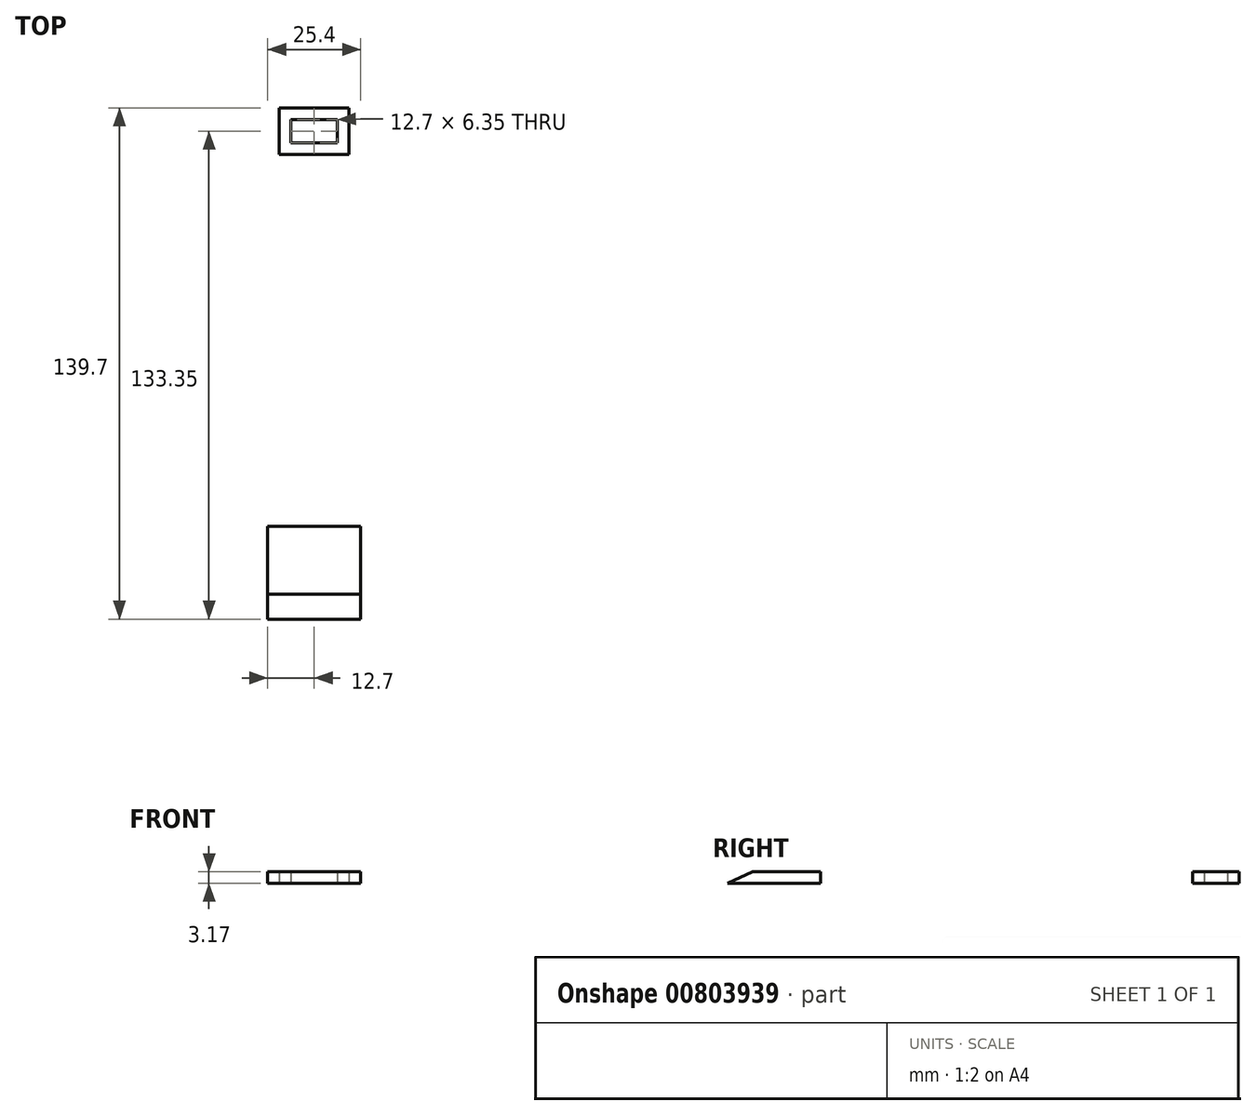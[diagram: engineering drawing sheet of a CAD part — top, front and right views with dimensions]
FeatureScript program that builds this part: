
annotation { "Feature Type Name" : "Feature", "Feature Type Description" : "" }
export const myFeature = defineFeature(function(context is Context, id is Id, definition is map)
    precondition{}
    {
        {
            var Q0;
            Q0=qCreatedBy(makeId("Top.planeOp"),FACE);
            var sketch = newSketch(context, id + "F0", { "sketchPlane" : qUnion([Q0])});
            skLineSegment(sketch, "E0", {"start": v(0, 139.7) * mm, "end": v(0, 0) * mm, "construction": true});
            skLineSegment(sketch, "E1.bottom", {"start": v(-12.7, 0) * mm, "end": v(12.7, 0) * mm});
            skLineSegment(sketch, "E1.top", {"start": v(-12.7, 25.4) * mm, "end": v(12.7, 25.4) * mm});
            skLineSegment(sketch, "E1.left", {"start": v(-12.7, 0) * mm, "end": v(-12.7, 25.4) * mm});
            skLineSegment(sketch, "E1.right", {"start": v(12.7, 0) * mm, "end": v(12.7, 25.4) * mm});
            skLineSegment(sketch, "E2.bottom", {"start": v(-6.35, 25.4) * mm, "end": v(6.35, 25.4) * mm});
            skLineSegment(sketch, "E2.top", {"start": v(-6.35, 127) * mm, "end": v(6.35, 127) * mm});
            skLineSegment(sketch, "E2.left", {"start": v(-6.35, 25.4) * mm, "end": v(-6.35, 127) * mm});
            skLineSegment(sketch, "E2.right", {"start": v(6.35, 25.4) * mm, "end": v(6.35, 127) * mm});
            skLineSegment(sketch, "E3.bottom", {"start": v(-9.53, 139.7) * mm, "end": v(9.53, 139.7) * mm});
            skLineSegment(sketch, "E3.top", {"start": v(-9.53, 127) * mm, "end": v(9.52, 127) * mm});
            skLineSegment(sketch, "E3.left", {"start": v(-9.53, 139.7) * mm, "end": v(-9.53, 127) * mm});
            skLineSegment(sketch, "E3.right", {"start": v(9.52, 139.7) * mm, "end": v(9.52, 127) * mm});
            skLineSegment(sketch, "E4.bottom", {"start": v(-6.35, 130.18) * mm, "end": v(6.35, 130.18) * mm});
            skLineSegment(sketch, "E4.top", {"start": v(-6.35, 136.52) * mm, "end": v(6.35, 136.52) * mm});
            skLineSegment(sketch, "E4.left", {"start": v(-6.35, 130.18) * mm, "end": v(-6.35, 136.52) * mm});
            skLineSegment(sketch, "E4.right", {"start": v(6.35, 130.18) * mm, "end": v(6.35, 136.52) * mm});
            skSolve(sketch);
        }
        {
            var Q0;
            Q0=makeQuery(id+"F0.imprint","IMPRINT",FACE,{"disambiguationData":[TD([[makeQuery(id+"F0.imprint","IMPRINT",EDGE,{"derivedFrom":sQuery(id+"F0.wireOp",EDGE,"E2.bottom")}),1.0]])]});
            var Q1;
            Q1=makeQuery(id+"F0.imprint","IMPRINT",FACE,{"disambiguationData":[TD([[makeQuery(id+"F0.imprint","IMPRINT",EDGE,{"derivedFrom":sQuery(id+"F0.wireOp",EDGE,"E3.bottom")}),-1.0]])]});
            var Q2;
            Q2=makeQuery(id+"F0.imprint","IMPRINT",FACE,{"disambiguationData":[TD([[makeQuery(id+"F0.imprint","IMPRINT",EDGE,{"derivedFrom":sQuery(id+"F0.wireOp",EDGE,"E1.bottom")}),1.0]])]});
            extrude(context, id + "F1", {"entities" : qUnion([Q0, Q1, Q2]), "depth" : 3.17 * mm, "offsetDistance" : 25.4 * mm});
        }
        {
            var Q0;
            Q0=makeQuery(id+"F1.opExtrude","SWEPT_FACE",FACE,{"disambiguationData":[OSD([sQuery(id+"F0.wireOp",EDGE,"E1.right")])]});
            var sketch = newSketch(context, id + "F2", { "sketchPlane" : qUnion([Q0])});
            skLineSegment(sketch, "E5", {"start": v(0, 0) * mm, "end": v(6.8, 3.18) * mm});
            skLineSegment(sketch, "E6", {"start": v(0, 0) * mm, "end": v(0, 3.18) * mm});
            skLineSegment(sketch, "E7", {"start": v(0, 3.17) * mm, "end": v(6.8, 3.17) * mm});
            skSolve(sketch);
        }
        {
            var Q0;
            Q0=makeQuery(id+"F2.imprint","IMPRINT",FACE,{"disambiguationData":[TD([[makeQuery(id+"F2.imprint","IMPRINT",EDGE,{"derivedFrom":sQuery(id+"F2.wireOp",EDGE,"E5")}),1.0]])]});
            extrude(context, id + "F3", {"entities" : qUnion([Q0]), "operationType" : NewBodyOperationType.REMOVE, "oppositeDirection" : true, "depth" : 25.4 * mm, "offsetDistance" : 25.4 * mm});
        }
    });
